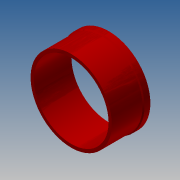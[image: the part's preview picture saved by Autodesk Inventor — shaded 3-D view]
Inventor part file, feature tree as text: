
AUTODESK INVENTOR PART (.ipt)
format: ipt  version: 2017.3 (Build 213257000, 257)  size: 120,832 bytes
history: native  units: in
note: dims shown in document units (in); Inventor stores cm internally (conversion verified against a paired STEP export)
features: other x3, extrude x2, sketch x2, chamfer x1
ambient origin geometry x8: Origin, YZ Plane, XZ Plane, XY Plane, X Axis, Y Axis, Z Axis, Center Point
bodies: Solid1 (feature_tree)
feature tree (8):
  other  "A1-19027-400-08 HCWI liner - pup.ipt"
  extrude  "Extrusion1"  Depth=0.5in TaperAngle=0.0deg
  extrude  "Extrusion2"  Depth=0.5in
  chamfer  "Chamfer1"  Distance=0.25in Angle=45.0deg
  other  "Solid1::A1-19027-400-08 HCWI liner - pup.ipt"
  other  "TaggingFeature1"
  sketch  "Sketch2"  dims[d0=0.3937in d1=0.5in d2=2.0in d3=0.0in d4=0.0in]
  sketch  "Sketch3"  dims[d5=0.5in d6=0.5in d7=0.0in d8=0.0in d9=0.25in d10=0.25in d11=0.125in d12=45.0deg]
